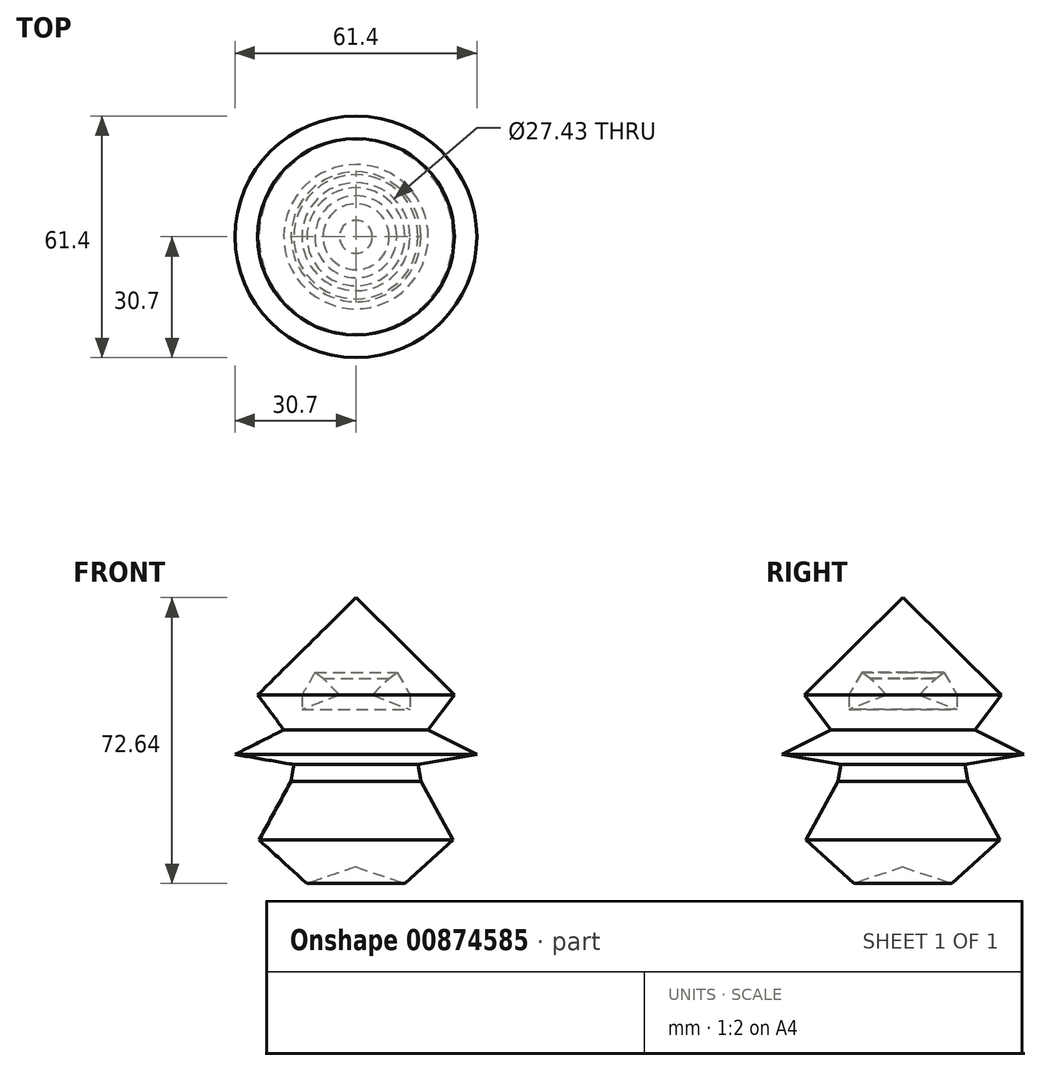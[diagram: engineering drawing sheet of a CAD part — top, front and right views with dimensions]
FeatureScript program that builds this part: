
annotation { "Feature Type Name" : "Feature", "Feature Type Description" : "" }
export const myFeature = defineFeature(function(context is Context, id is Id, definition is map)
    precondition{}
    {
        {
            var Q0;
            Q0=qCreatedBy(makeId("Front.planeOp"),FACE);
            var sketch = newSketch(context, id + "F0", { "sketchPlane" : qUnion([Q0])});
            skLineSegment(sketch, "E0", {"start": v(0, 0) * mm, "end": v(0, 53.56) * mm});
            skLineSegment(sketch, "E1", {"start": v(0, 53.56) * mm, "end": v(24.98, 28.85) * mm});
            skLineSegment(sketch, "E2", {"start": v(16.5, 6.91) * mm, "end": v(24.61, -8.02) * mm});
            skLineSegment(sketch, "E3", {"start": v(24.61, -8.02) * mm, "end": v(12.44, -19.08) * mm});
            skLineSegment(sketch, "E4", {"start": v(12.44, -19.08) * mm, "end": v(0, -14.84) * mm});
            skLineSegment(sketch, "E5", {"start": v(0, -14.84) * mm, "end": v(0, 0) * mm});
            skLineSegment(sketch, "E6", {"start": v(8.39, 33.1) * mm, "end": v(4.17, 28.83) * mm});
            skLineSegment(sketch, "E7", {"start": v(4.17, 28.83) * mm, "end": v(13.71, 25.14) * mm});
            skLineSegment(sketch, "E8", {"start": v(13.71, 25.14) * mm, "end": v(13.71, 28.83) * mm});
            skLineSegment(sketch, "E9", {"start": v(13.71, 28.83) * mm, "end": v(10.42, 34.57) * mm});
            skLineSegment(sketch, "E10", {"start": v(10.42, 34.57) * mm, "end": v(8.39, 33.1) * mm});
            skLineSegment(sketch, "E11", {"start": v(24.98, 28.85) * mm, "end": v(18.34, 20) * mm});
            skLineSegment(sketch, "E12", {"start": v(18.34, 20) * mm, "end": v(30.7, 13.73) * mm});
            skLineSegment(sketch, "E13", {"start": v(30.7, 13.73) * mm, "end": v(15.76, 11.15) * mm});
            skLineSegment(sketch, "E14", {"start": v(15.76, 11.15) * mm, "end": v(16.5, 6.91) * mm});
            skSolve(sketch);
        }
        {
            var Q0;
            Q0 = qSketchRegion(id + "F0", true);
            var Q1;
            Q1=sQuery(id+"F0.wireOp",EDGE,"E0");
            revolve(context, id + "F1", {"surfaceOperationType" : NewSurfaceOperationType.NEW, "entities" : qUnion([Q0]), "axis" : qUnion([Q1]), "revolveType" : RevolveType.FULL});
        }
    });
